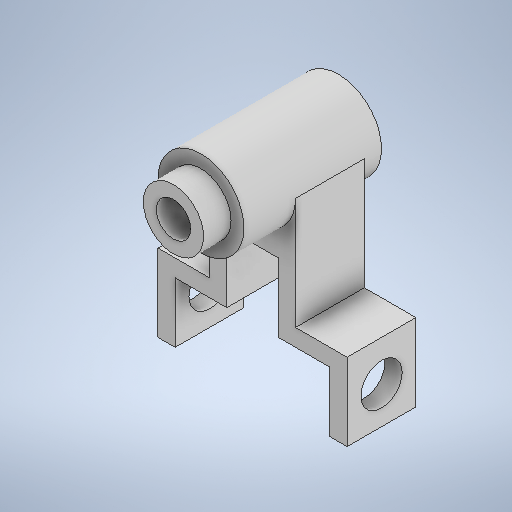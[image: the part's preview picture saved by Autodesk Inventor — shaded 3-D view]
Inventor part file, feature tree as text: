
AUTODESK INVENTOR PART (.ipt)
format: ipt  version: 2025.2 (Build 292293000, 293)  size: 492,544 bytes
history: native  units: in
note: dims shown in document units (in); Inventor stores cm internally (conversion verified against a paired STEP export)
features: sketch x5, extrude x4, other x1
ambient origin geometry x8: Origin, YZ Plane, XZ Plane, XY Plane, X Axis, Y Axis, Z Axis, Center Point
bodies: Solid1 (feature_tree)
feature tree (10):
  extrude  "Extrusion1"  Depth=1.9685in
  extrude  "Extrusion2"  Depth=3.5433in
  extrude  "Extrusion3"  Depth=1.7717in
  sketch  "Sketch4"  dims[d24=1.5748in d25=0.0in d26=1.9685in]
  extrude  "Extrusion4"  Depth=1.9685in
  sketch  "Sketch1"  dims[d3=1.9685in d4=2.5591in]
  other  "Image1"
  sketch  "Sketch2"  dims[d15=0.9843in d16=3.5433in]
  sketch  "Sketch3"  dims[d18=1.1811in d19=1.7717in]
  sketch  "Sketch5"  dims[d27=1.1811in d28=1.9685in d29=0.0in d30=0.0in d31=1.378in d32=0.7874in d33=0.6299in d34=0.0in d35=0.9449in d36=0.7874in d37=4.7244in d38=0.0in]
